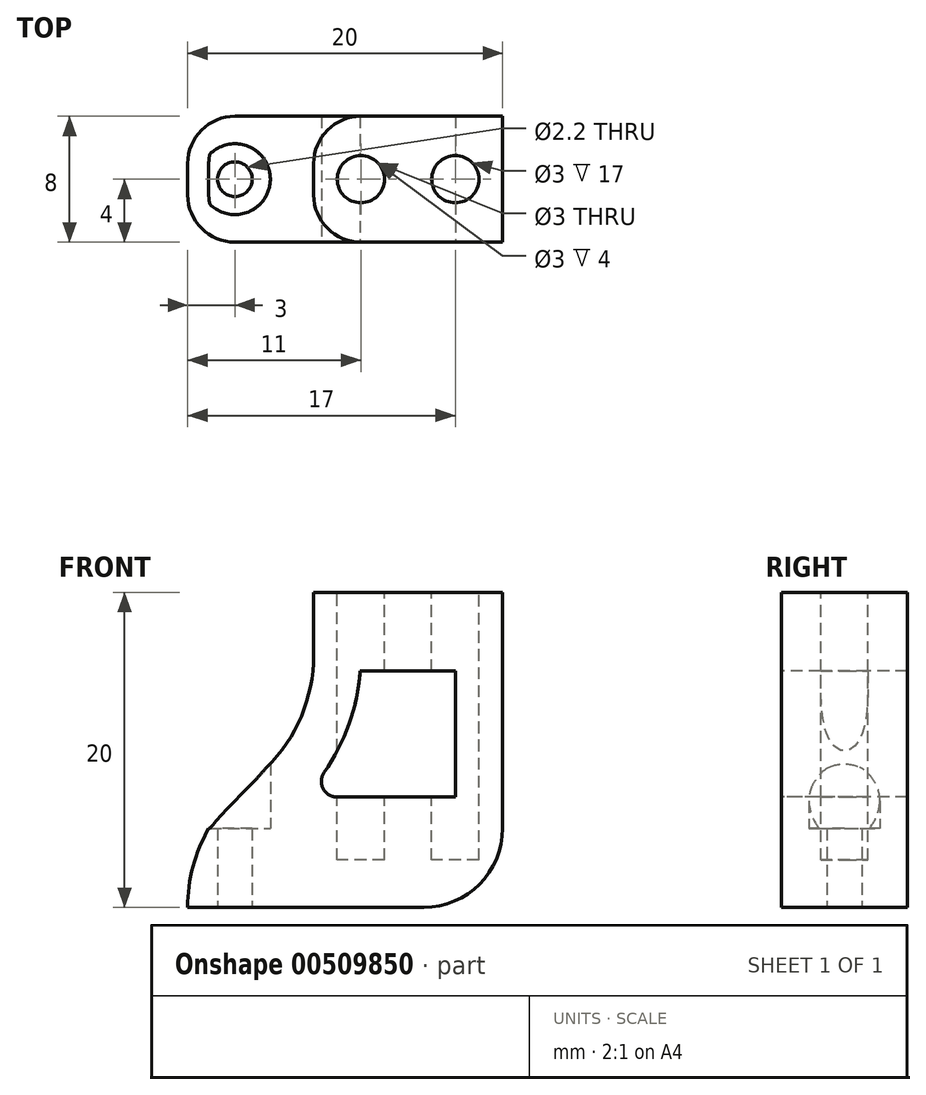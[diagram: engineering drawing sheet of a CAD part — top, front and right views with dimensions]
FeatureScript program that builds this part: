
annotation { "Feature Type Name" : "Feature", "Feature Type Description" : "" }
export const myFeature = defineFeature(function(context is Context, id is Id, definition is map)
    precondition{}
    {
        {
            var Q0;
            Q0=qCreatedBy(makeId("Front.planeOp"),FACE);
            var sketch = newSketch(context, id + "F0", { "sketchPlane" : qUnion([Q0])});
            skLineSegment(sketch, "E0.bottom", {"start": v(0, 0) * mm, "end": v(20, 0) * mm});
            skLineSegment(sketch, "E0.top", {"start": v(6.67, 10) * mm, "end": v(20, 10) * mm});
            skLineSegment(sketch, "E0.left", {"start": v(0, 0) * mm, "end": v(0, 5) * mm});
            skLineSegment(sketch, "E0.right", {"start": v(20, 0) * mm, "end": v(20, 10) * mm});
            skLineSegment(sketch, "E1", {"start": v(0, 5) * mm, "end": v(20, 20) * mm});
            skLineSegment(sketch, "E2", {"start": v(20, 20) * mm, "end": v(20, 10) * mm});
            skLineSegment(sketch, "E3", {"start": v(20, 20) * mm, "end": v(8, 20) * mm});
            skLineSegment(sketch, "E4", {"start": v(8, 20) * mm, "end": v(8, 11) * mm});
            skPoint(sketch, "E5.orphan", {"position": v(0, 10) * mm});
            skSolve(sketch);
        }
        {
            var Q0;
            Q0 = qSketchRegion(id + "F0", true);
            extrude(context, id + "F1", {"entities" : qUnion([Q0]), "depth" : 8 * mm, "offsetDistance" : 25 * mm});
        }
        {
            var Q0;
            Q0=makeQuery(id+"F1.opExtrude","SWEPT_FACE",FACE,{"disambiguationData":[OSD([sQuery(id+"F0.wireOp",EDGE,"E0.bottom")])]});
            var sketch = newSketch(context, id + "F2", { "sketchPlane" : qUnion([Q0])});
            skCircle(sketch, "E6", {"center": v(3, 4) * mm, "radius": 1.1 * mm});
            skPoint(sketch, "E6.centerSnap0", {"position": v(0, 4) * mm});
            skSolve(sketch);
        }
        {
            var Q0;
            Q0=makeQuery(id+"F1.opExtrude","SWEPT_FACE",FACE,{"disambiguationData":[OSD([sQuery(id+"F0.wireOp",EDGE,"E3")])]});
            var sketch = newSketch(context, id + "F3", { "sketchPlane" : qUnion([Q0])});
            skCircle(sketch, "E7", {"center": v(11, -4) * mm, "radius": 1.5 * mm});
            skPoint(sketch, "E7.centerSnap0", {"position": v(8, -4) * mm});
            skCircle(sketch, "E8", {"center": v(17, -4) * mm, "radius": 1.5 * mm});
            skSolve(sketch);
        }
        {
            var Q0;
            Q0 = qSketchRegion(id + "F3", true);
            extrude(context, id + "F4", {"entities" : qUnion([Q0]), "operationType" : NewBodyOperationType.REMOVE, "oppositeDirection" : true, "depth" : 17 * mm, "offsetDistance" : 25 * mm});
        }
        {
            var Q0;
            Q0=makeQuery(id+"F1.opExtrude","SWEPT_EDGE",EDGE,{"disambiguationData":[OSD([sQuery(id+"F0.wireOp",EDGE,"E0.left"),sQuery(id+"F0.wireOp",EDGE,"E1")])]});
            var Q1;
            Q1=makeQuery(id+"F1.opExtrude","SWEPT_EDGE",EDGE,{"disambiguationData":[OSD([sQuery(id+"F0.wireOp",EDGE,"E1"),sQuery(id+"F0.wireOp",EDGE,"E4")])]});
            fillet(context, id + "F5", {"entities" : qUnion([Q0, Q1]), "radius" : 10 * mm, "tangentPropagation" : true, "allowEdgeOverflow" : false});
        }
        {
            var Q0;
            Q0=makeQuery(id+"F1.opExtrude","SWEPT_EDGE",EDGE,{"disambiguationData":[OSD([sQuery(id+"F0.wireOp",EDGE,"E0.bottom"),sQuery(id+"F0.wireOp",EDGE,"E0.right")])]});
            fillet(context, id + "F6", {"entities" : qUnion([Q0]), "radius" : 5 * mm, "tangentPropagation" : true, "allowEdgeOverflow" : false});
        }
        {
            var Q0;
            Q0=makeQuery(id+"F1.opExtrude","CAP_FACE",FACE,{"disambiguationData":[OSD([sQuery(id+"F0.wireOp",EDGE,"E0.bottom"),sQuery(id+"F0.wireOp",EDGE,"E0.left"),sQuery(id+"F0.wireOp",EDGE,"E0.right"),sQuery(id+"F0.wireOp",EDGE,"E1"),sQuery(id+"F0.wireOp",EDGE,"E2"),sQuery(id+"F0.wireOp",EDGE,"E3"),sQuery(id+"F0.wireOp",EDGE,"E4")])],"isStart":false});
            var sketch = newSketch(context, id + "F7", { "sketchPlane" : qUnion([Q0])});
            skArc(sketch, "E9.1", {"start": v(10.96, 15) * mm, "mid": v(10.24, 11.63) * mm, "end": v(8.67, 8.57) * mm});
            skLineSegment(sketch, "E9.3", {"start": v(17, 7) * mm, "end": v(17, 15) * mm});
            skLineSegment(sketch, "E10", {"start": v(17, 7) * mm, "end": v(9.49, 7) * mm});
            skPoint(sketch, "E11.visualSharp", {"position": v(7.38, 7) * mm});
            skArc(sketch, "E11.filletArc", {"start": v(8.67, 8.57) * mm, "mid": v(8.6, 7.54) * mm, "end": v(9.49, 7) * mm});
            skLineSegment(sketch, "E12", {"start": v(17, 15) * mm, "end": v(10.96, 15) * mm});
            skSolve(sketch);
        }
        {
            var Q0;
            Q0 = qSketchRegion(id + "F7", true);
            extrude(context, id + "F8", {"entities" : qUnion([Q0]), "operationType" : NewBodyOperationType.REMOVE, "endBound" : BoundingType.UP_TO_NEXT, "oppositeDirection" : true, "depth" : 25 * mm, "offsetDistance" : 25 * mm});
        }
        {
            var Q0;
            {var subQ0=sQuery(id+"F0.wireOp",EDGE,"E1");var subQ1=sQuery(id+"F0.wireOp",EDGE,"E0.left");Q0=makeQuery(id+"F5.opFillet","BLEND_EDGE",EDGE,{"blendedFrom":[makeQuery(id+"F1.opExtrude","SWEPT_EDGE",EDGE,{"disambiguationData":[OSD([subQ1,subQ0])]}),makeQuery(id+"F1.opExtrude","CAP_FACE",FACE,{"disambiguationData":[OSD([sQuery(id+"F0.wireOp",EDGE,"E0.bottom"),subQ1,sQuery(id+"F0.wireOp",EDGE,"E0.right"),subQ0,sQuery(id+"F0.wireOp",EDGE,"E2"),sQuery(id+"F0.wireOp",EDGE,"E3"),sQuery(id+"F0.wireOp",EDGE,"E4")])],"isStart":false})],"blendedInto":[makeQuery(id+"F1.opExtrude","CAP_FACE",FACE,{"disambiguationData":[OSD([sQuery(id+"F0.wireOp",EDGE,"E0.bottom"),subQ1,sQuery(id+"F0.wireOp",EDGE,"E0.right"),subQ0,sQuery(id+"F0.wireOp",EDGE,"E2"),sQuery(id+"F0.wireOp",EDGE,"E3"),sQuery(id+"F0.wireOp",EDGE,"E4")])],"isStart":false})]});}
            var Q1;
            {var subQ0=sQuery(id+"F0.wireOp",EDGE,"E1");var subQ1=sQuery(id+"F0.wireOp",EDGE,"E0.left");Q1=makeQuery(id+"F5.opFillet","BLEND_EDGE",EDGE,{"blendedFrom":[makeQuery(id+"F1.opExtrude","SWEPT_EDGE",EDGE,{"disambiguationData":[OSD([subQ1,subQ0])]}),makeQuery(id+"F1.opExtrude","CAP_FACE",FACE,{"disambiguationData":[OSD([sQuery(id+"F0.wireOp",EDGE,"E0.bottom"),subQ1,sQuery(id+"F0.wireOp",EDGE,"E0.right"),subQ0,sQuery(id+"F0.wireOp",EDGE,"E2"),sQuery(id+"F0.wireOp",EDGE,"E3"),sQuery(id+"F0.wireOp",EDGE,"E4")])],"isStart":true})],"blendedInto":[makeQuery(id+"F1.opExtrude","CAP_FACE",FACE,{"disambiguationData":[OSD([sQuery(id+"F0.wireOp",EDGE,"E0.bottom"),subQ1,sQuery(id+"F0.wireOp",EDGE,"E0.right"),subQ0,sQuery(id+"F0.wireOp",EDGE,"E2"),sQuery(id+"F0.wireOp",EDGE,"E3"),sQuery(id+"F0.wireOp",EDGE,"E4")])],"isStart":true})]});}
            fillet(context, id + "F9", {"entities" : qUnion([Q0, Q1]), "radius" : 3 * mm, "tangentPropagation" : true, "allowEdgeOverflow" : false});
        }
        {
            var Q0;
            Q0 = qSketchRegion(id + "F2", true);
            extrude(context, id + "F10", {"entities" : qUnion([Q0]), "operationType" : NewBodyOperationType.REMOVE, "oppositeDirection" : true, "depth" : 25 * mm, "offsetDistance" : 25 * mm});
        }
        {
            var Q0;
            Q0=qCreatedBy(makeId("Top.planeOp"),FACE);
            cPlane(context, id + "F11", {"entities" : qUnion([Q0]), "cplaneType" : CPlaneType.OFFSET, "offset" : 5 * mm, "width" : 150 * mm, "height" : 150 * mm});
        }
        {
            var Q0;
            Q0=qCreatedBy(id+"F11.planeOp",FACE);
            var sketch = newSketch(context, id + "F12", { "sketchPlane" : qUnion([Q0])});
            skCircle(sketch, "E13", {"center": v(3, -4) * mm, "radius": 2.25 * mm});
            skSolve(sketch);
        }
        {
            var Q0;
            Q0 = qSketchRegion(id + "F12", true);
            extrude(context, id + "F13", {"entities" : qUnion([Q0]), "operationType" : NewBodyOperationType.REMOVE, "depth" : 25 * mm, "offsetDistance" : 25 * mm});
        }
    });
